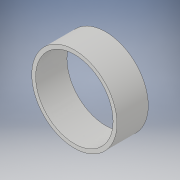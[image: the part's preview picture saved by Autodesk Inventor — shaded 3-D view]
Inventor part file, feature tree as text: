
AUTODESK INVENTOR PART (.ipt)
format: ipt  version: 2019 (Build 230136000, 136)  size: 103,424 bytes
history: native  units: mm
features: extrude x2, sketch x2
ambient origin geometry x8: Origin, YZ Plane, XZ Plane, XY Plane, X Axis, Y Axis, Z Axis, Center Point
bodies: Solid1 (feature_tree)
feature tree (4):
  extrude  "Extrusion1"  Depth=3.46mm TaperAngle=0.0deg
  extrude  "Extrusion2"  Depth=3.46mm TaperAngle=0.0deg
  sketch  "Sketch1"  dims[d0=9.42mm d1=3.46mm d2=0.0mm]
  sketch  "Sketch2"  dims[d3=8.56mm d4=3.46mm d5=0.0mm]
